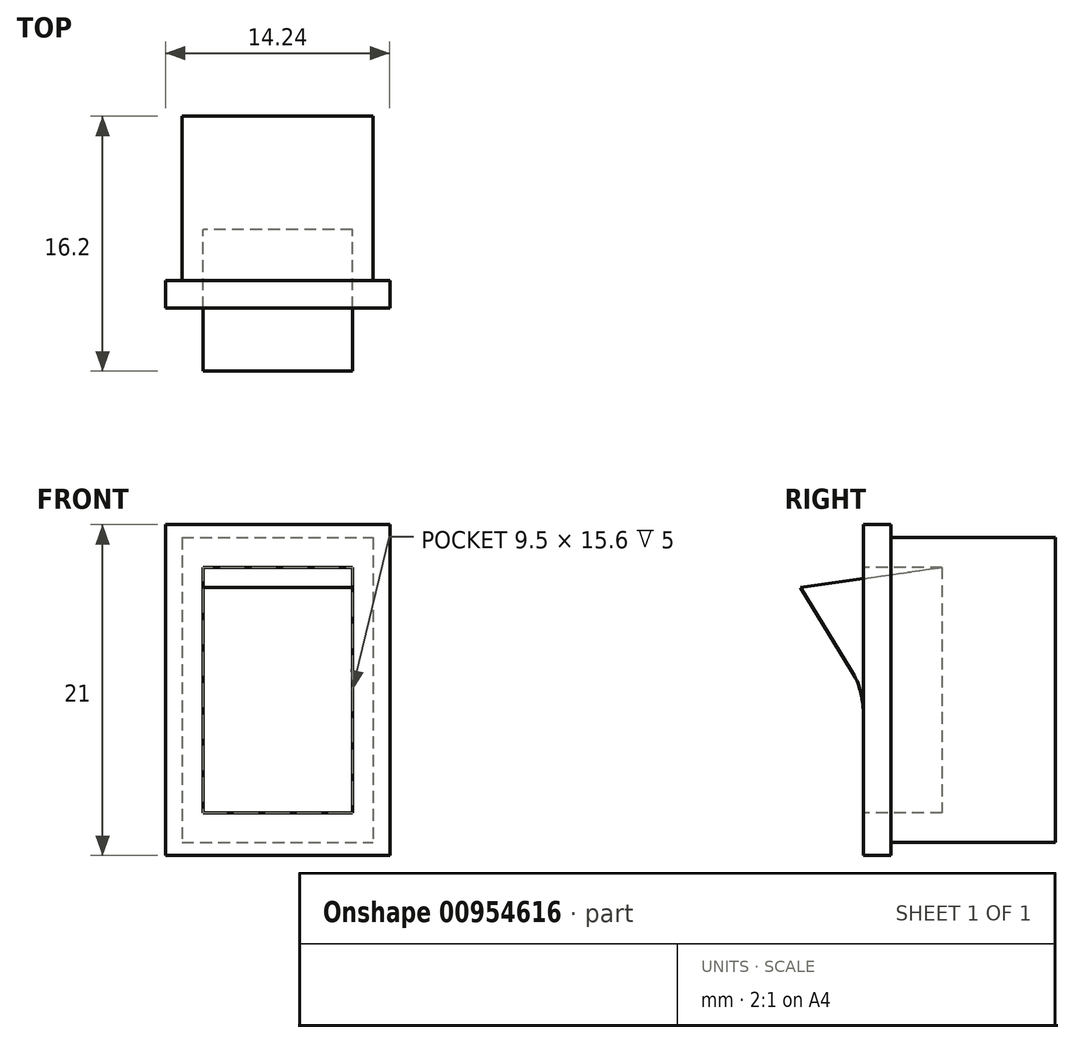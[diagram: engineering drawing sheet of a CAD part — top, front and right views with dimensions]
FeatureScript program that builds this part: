
annotation { "Feature Type Name" : "Feature", "Feature Type Description" : "" }
export const myFeature = defineFeature(function(context is Context, id is Id, definition is map)
    precondition{}
    {
        {
            var Q0;
            Q0=qCreatedBy(makeId("Front.planeOp"),FACE);
            var sketch = newSketch(context, id + "F0", { "sketchPlane" : qUnion([Q0])});
            skLineSegment(sketch, "E0.bottom", {"start": v(-6.07, 9.69) * mm, "end": v(6.08, 9.69) * mm});
            skLineSegment(sketch, "E0.top", {"start": v(-6.08, -9.7) * mm, "end": v(6.07, -9.7) * mm});
            skLineSegment(sketch, "E0.left", {"start": v(-6.07, 9.69) * mm, "end": v(-6.08, -9.7) * mm});
            skLineSegment(sketch, "E0.right", {"start": v(6.08, 9.69) * mm, "end": v(6.07, -9.7) * mm});
            skPoint(sketch, "E0.middle", {"position": v(0, 0) * mm});
            skSolve(sketch);
        }
        {
            var Q0;
            Q0=qSketchRegion(id+"F0",true);
            extrude(context, id + "F1", {"entities" : qUnion([Q0]), "depth" : 10.45 * mm, "offsetDistance" : 25 * mm});
        }
        {
            var Q0;
            Q0=makeQuery(id+"F1.opExtrude","CAP_FACE",FACE,{"disambiguationData":[OSD([sQuery(id+"F0.wireOp",EDGE,"E0.bottom"),sQuery(id+"F0.wireOp",EDGE,"E0.top"),sQuery(id+"F0.wireOp",EDGE,"E0.left"),sQuery(id+"F0.wireOp",EDGE,"E0.right")])],"isStart":false});
            var sketch = newSketch(context, id + "F2", { "sketchPlane" : qUnion([Q0])});
            skLineSegment(sketch, "E1.bottom", {"start": v(-7.12, 10.5) * mm, "end": v(7.13, 10.5) * mm});
            skLineSegment(sketch, "E1.top", {"start": v(-7.13, -10.5) * mm, "end": v(7.12, -10.5) * mm});
            skLineSegment(sketch, "E1.left", {"start": v(-7.12, 10.5) * mm, "end": v(-7.13, -10.5) * mm});
            skLineSegment(sketch, "E1.right", {"start": v(7.13, 10.5) * mm, "end": v(7.12, -10.5) * mm});
            skPoint(sketch, "E1.middle", {"position": v(0, 0) * mm});
            skSolve(sketch);
        }
        {
            var Q0;
            Q0=qSketchRegion(id+"F2",true);
            extrude(context, id + "F3", {"entities" : qUnion([Q0]), "operationType" : NewBodyOperationType.ADD, "depth" : 1.75 * mm, "offsetDistance" : 25 * mm});
        }
        {
            var Q0;
            Q0=makeQuery(id+"F3.opExtrude","CAP_FACE",FACE,{"disambiguationData":[OSD([sQuery(id+"F2.wireOp",EDGE,"E1.bottom"),sQuery(id+"F2.wireOp",EDGE,"E1.top"),sQuery(id+"F2.wireOp",EDGE,"E1.left"),sQuery(id+"F2.wireOp",EDGE,"E1.right")])],"isStart":false});
            var sketch = newSketch(context, id + "F4", { "sketchPlane" : qUnion([Q0])});
            skLineSegment(sketch, "E2.bottom", {"start": v(-4.75, 7.8) * mm, "end": v(4.75, 7.8) * mm});
            skLineSegment(sketch, "E2.top", {"start": v(-4.75, -7.8) * mm, "end": v(4.75, -7.8) * mm});
            skLineSegment(sketch, "E2.left", {"start": v(-4.75, 7.8) * mm, "end": v(-4.75, -7.8) * mm});
            skLineSegment(sketch, "E2.right", {"start": v(4.75, 7.8) * mm, "end": v(4.75, -7.8) * mm});
            skPoint(sketch, "E2.middle", {"position": v(0, 0) * mm});
            skSolve(sketch);
        }
        {
            var Q0;
            Q0=qSketchRegion(id+"F4",true);
            extrude(context, id + "F5", {"entities" : qUnion([Q0]), "operationType" : NewBodyOperationType.REMOVE, "oppositeDirection" : true, "depth" : 5 * mm, "offsetDistance" : 25 * mm});
        }
        {
            var Q0;
            Q0=makeQuery(id+"F5.boolean.opBoolean","COPY",FACE,{"derivedFrom":makeQuery(id+"F5.opExtrude","SWEPT_FACE",FACE,{"disambiguationData":[OSD([sQuery(id+"F4.wireOp",EDGE,"E2.left")])]})});
            var sketch = newSketch(context, id + "F6", { "sketchPlane" : qUnion([Q0])});
            skLineSegment(sketch, "E3", {"start": v(-12.2, -7.8) * mm, "end": v(-12.2, -1.42) * mm});
            skLineSegment(sketch, "E4", {"start": v(-12.94, 1.2) * mm, "end": v(-16.2, 6.5) * mm});
            skLineSegment(sketch, "E5", {"start": v(-16.2, 6.5) * mm, "end": v(-7.2, 7.8) * mm});
            skLineSegment(sketch, "E6", {"start": v(-7.2, 7.8) * mm, "end": v(-7.2, -7.8) * mm});
            skLineSegment(sketch, "E7", {"start": v(-7.2, -7.8) * mm, "end": v(-12.2, -7.8) * mm});
            skPoint(sketch, "E8.visualSharp", {"position": v(-12.2, 0) * mm});
            skArc(sketch, "E8.filletArc", {"start": v(-12.2, -1.42) * mm, "mid": v(-12.39, -0.05) * mm, "end": v(-12.94, 1.2) * mm});
            skSolve(sketch);
        }
        {
            var Q0;
            Q0=qSketchRegion(id+"F6",true);
            extrude(context, id + "F7", {"entities" : qUnion([Q0]), "depth" : 9.5 * mm, "offsetDistance" : 25 * mm});
        }
    });
